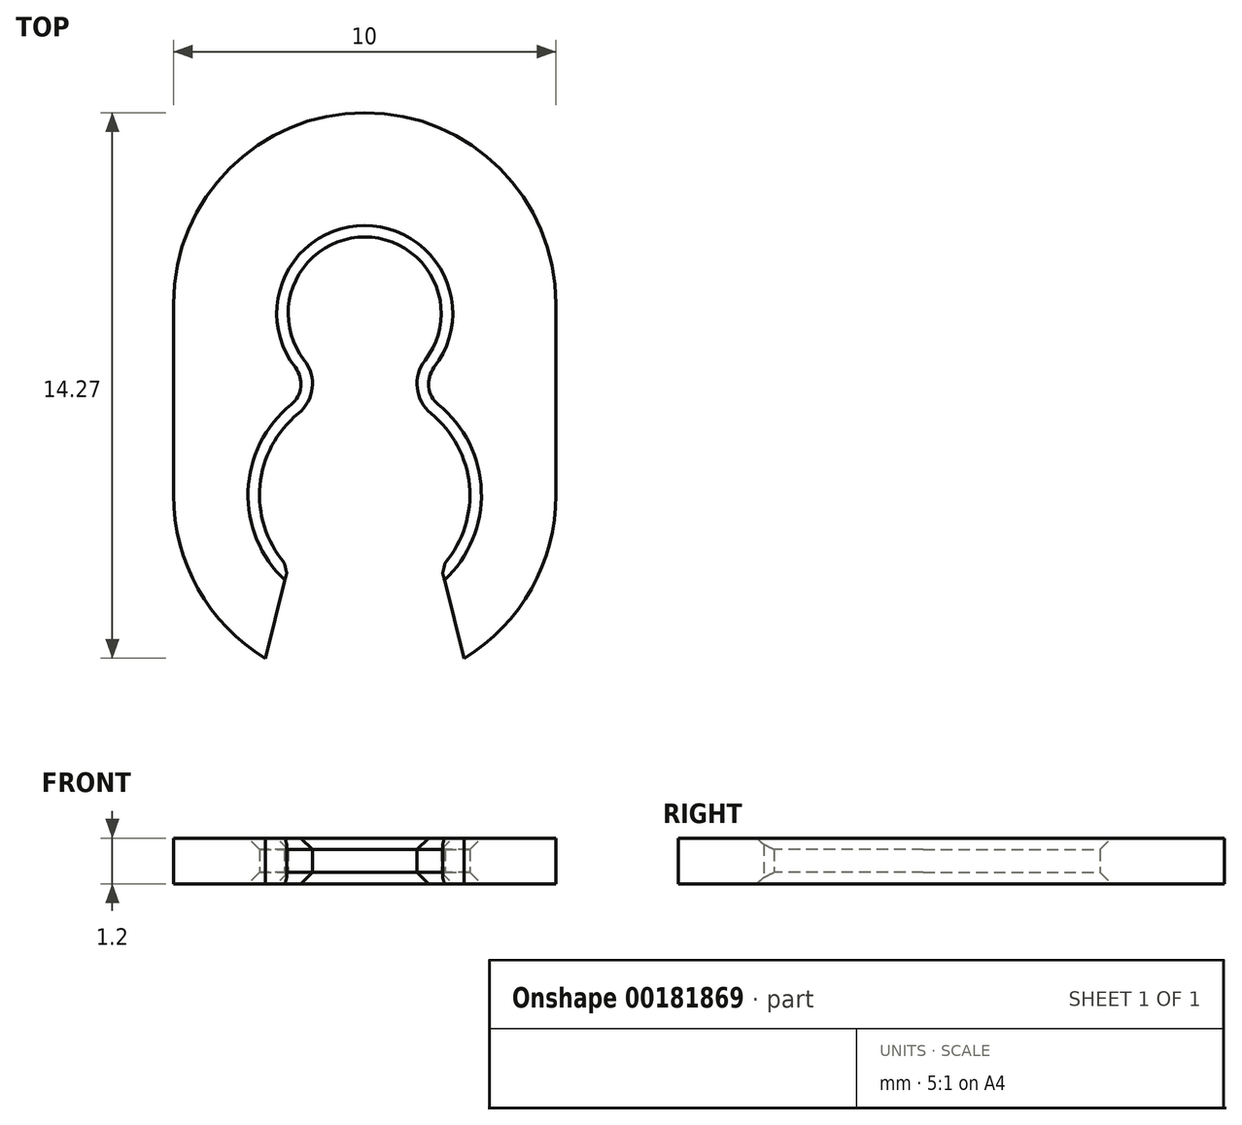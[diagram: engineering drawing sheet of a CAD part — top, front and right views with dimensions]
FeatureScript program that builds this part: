
annotation { "Feature Type Name" : "Feature", "Feature Type Description" : "" }
export const myFeature = defineFeature(function(context is Context, id is Id, definition is map)
    precondition{}
    {
        {
            var Q0;
            Q0=qCreatedBy(makeId("Top.planeOp"),FACE);
            var sketch = newSketch(context, id + "F0", { "sketchPlane" : qUnion([Q0])});
            skCircle(sketch, "E0", {"center": v(0, 0) * mm, "radius": 2.75 * mm});
            skCircle(sketch, "E1", {"center": v(0, 0) * mm, "radius": 5 * mm});
            skCircle(sketch, "E2", {"center": v(0, 4.75) * mm, "radius": 2 * mm});
            skArc(sketch, "E3", {"start": v(1.58, 3.52) * mm, "mid": v(1.37, 2.8) * mm, "end": v(1.74, 2.13) * mm});
            skArc(sketch, "E4", {"start": v(-1.74, 2.13) * mm, "mid": v(-1.37, 2.8) * mm, "end": v(-1.58, 3.52) * mm});
            skLineSegment(sketch, "E5", {"start": v(-5, 0) * mm, "end": v(-5, 5) * mm});
            skLineSegment(sketch, "E6", {"start": v(5, 0) * mm, "end": v(5, 5) * mm});
            skArc(sketch, "E7", {"start": v(-5, 5) * mm, "mid": v(0, 10) * mm, "end": v(5, 5) * mm});
            skLineSegment(sketch, "E8", {"start": v(-2, -1.89) * mm, "end": v(-2.6, -4.27) * mm});
            skLineSegment(sketch, "E9", {"start": v(2, -1.89) * mm, "end": v(2.6, -4.27) * mm});
            skLineSegment(sketch, "E10", {"start": v(0, 0) * mm, "end": v(-2, -1.89) * mm, "construction": true});
            skLineSegment(sketch, "E11", {"start": v(2, -1.89) * mm, "end": v(0, 0) * mm, "construction": true});
            skLineSegment(sketch, "E12", {"start": v(2, -1.89) * mm, "end": v(2, -4.58) * mm, "construction": true});
            skLineSegment(sketch, "E13", {"start": v(-2, -1.89) * mm, "end": v(-2, -4.58) * mm, "construction": true});
            skSolve(sketch);
        }
        {
            var Q0;
            {var subQ0=sQuery(id+"F0.wireOp",EDGE,"E4");Q0=makeQuery(id+"F0.imprint","IMPRINT",FACE,{"disambiguationData":[TD([[makeQuery(id+"F0.imprint","IMPRINT",EDGE,{"derivedFrom":subQ0}),1.0]])]});}
            var Q1;
            {var subQ0=sQuery(id+"F0.wireOp",EDGE,"E3");Q1=makeQuery(id+"F0.imprint","IMPRINT",FACE,{"disambiguationData":[TD([[makeQuery(id+"F0.imprint","IMPRINT",EDGE,{"derivedFrom":subQ0}),1.0]])]});}
            var Q2;
            {var subQ0=sQuery(id+"F0.wireOp",EDGE,"E5");Q2=makeQuery(id+"F0.imprint","IMPRINT",FACE,{"disambiguationData":[TD([[makeQuery(id+"F0.imprint","IMPRINT",EDGE,{"derivedFrom":subQ0}),-1.0]])]});}
            extrude(context, id + "F1", {"entities" : qUnion([Q0, Q1, Q2]), "depth" : 1.2 * mm});
        }
        {
            var Q0;
            {var subQ0=sQuery(id+"F0.wireOp",EDGE,"E0");Q0=makeQuery(id+"F1.opExtrude","CAP_EDGE",EDGE,{"disambiguationData":[OSD([subQ0]),TDD([makeQuery(id+"F0.imprint","IMPRINT",EDGE,{"disambiguationData":[TD([[makeQuery(id+"F0.imprint","INTERSECT",VERTEX,{"derivedFrom":[subQ0,sQuery(id+"F0.wireOp",EDGE,"E4")]}),-1.0]])],"derivedFrom":subQ0})])],"isStart":false});}
            var Q1;
            {var subQ0=sQuery(id+"F0.wireOp",EDGE,"E0");Q1=makeQuery(id+"F1.opExtrude","CAP_EDGE",EDGE,{"disambiguationData":[OSD([subQ0]),TDD([makeQuery(id+"F0.imprint","IMPRINT",EDGE,{"disambiguationData":[TD([[makeQuery(id+"F0.imprint","INTERSECT",VERTEX,{"derivedFrom":[subQ0,sQuery(id+"F0.wireOp",EDGE,"E4")]}),-1.0]])],"derivedFrom":subQ0})])],"isStart":true});}
            var Q2;
            Q2=makeQuery(id+"F1.opExtrude","SWEPT_EDGE",EDGE,{"disambiguationData":[OSD([sQuery(id+"F0.wireOp",EDGE,"E0"),sQuery(id+"F0.wireOp",EDGE,"E8")])]});
            var Q3;
            Q3=makeQuery(id+"F1.opExtrude","SWEPT_EDGE",EDGE,{"disambiguationData":[OSD([sQuery(id+"F0.wireOp",EDGE,"E0"),sQuery(id+"F0.wireOp",EDGE,"E9")])]});
            var Q4;
            {var subQ0=sQuery(id+"F0.wireOp",EDGE,"E0");Q4=makeQuery(id+"F1.opExtrude","CAP_EDGE",EDGE,{"disambiguationData":[OSD([subQ0]),TDD([makeQuery(id+"F0.imprint","IMPRINT",EDGE,{"disambiguationData":[TD([[makeQuery(id+"F0.imprint","INTERSECT",VERTEX,{"derivedFrom":[subQ0,sQuery(id+"F0.wireOp",EDGE,"E3")]}),1.0]])],"derivedFrom":subQ0})])],"isStart":false});}
            var Q5;
            {var subQ0=sQuery(id+"F0.wireOp",EDGE,"E0");Q5=makeQuery(id+"F1.opExtrude","CAP_EDGE",EDGE,{"disambiguationData":[OSD([subQ0]),TDD([makeQuery(id+"F0.imprint","IMPRINT",EDGE,{"disambiguationData":[TD([[makeQuery(id+"F0.imprint","INTERSECT",VERTEX,{"derivedFrom":[subQ0,sQuery(id+"F0.wireOp",EDGE,"E3")]}),1.0]])],"derivedFrom":subQ0})])],"isStart":true});}
            var Q6;
            Q6=makeQuery(id+"F1.opExtrude","CAP_EDGE",EDGE,{"disambiguationData":[OSD([sQuery(id+"F0.wireOp",EDGE,"E2")])],"isStart":false});
            var Q7;
            Q7=makeQuery(id+"F1.opExtrude","CAP_EDGE",EDGE,{"disambiguationData":[OSD([sQuery(id+"F0.wireOp",EDGE,"E2")])],"isStart":true});
            var Q8;
            Q8=makeQuery(id+"F1.opExtrude","CAP_EDGE",EDGE,{"disambiguationData":[OSD([sQuery(id+"F0.wireOp",EDGE,"E4")])],"isStart":false});
            var Q9;
            Q9=makeQuery(id+"F1.opExtrude","CAP_EDGE",EDGE,{"disambiguationData":[OSD([sQuery(id+"F0.wireOp",EDGE,"E4")])],"isStart":true});
            var Q10;
            Q10=makeQuery(id+"F1.opExtrude","CAP_EDGE",EDGE,{"disambiguationData":[OSD([sQuery(id+"F0.wireOp",EDGE,"E3")])],"isStart":false});
            var Q11;
            Q11=makeQuery(id+"F1.opExtrude","CAP_EDGE",EDGE,{"disambiguationData":[OSD([sQuery(id+"F0.wireOp",EDGE,"E3")])],"isStart":true});
            chamfer(context, id + "F2", {"entities" : qUnion([Q0, Q1, Q2, Q3, Q4, Q5, Q6, Q7, Q8, Q9, Q10, Q11]), "width" : 0.3 * mm});
        }
    });
